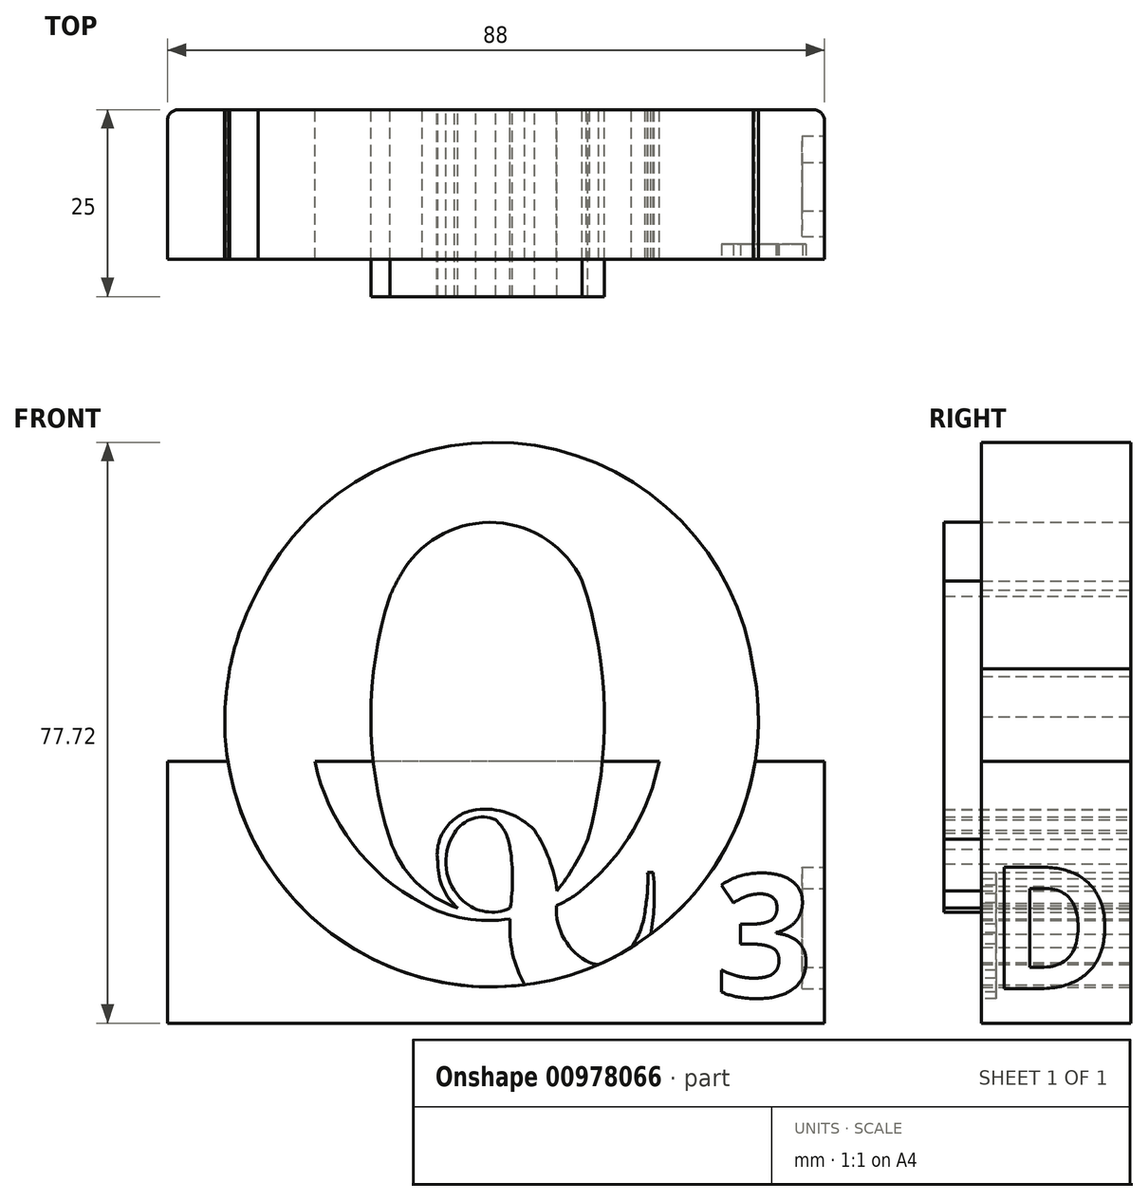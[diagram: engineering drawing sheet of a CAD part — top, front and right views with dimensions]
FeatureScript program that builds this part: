
annotation { "Feature Type Name" : "Feature", "Feature Type Description" : "" }
export const myFeature = defineFeature(function(context is Context, id is Id, definition is map)
    precondition{}
    {
        {
            var Q0;
            Q0=qCreatedBy(makeId("Front.planeOp"),FACE);
            var sketch = newSketch(context, id + "F0", { "sketchPlane" : qUnion([Q0])});
            skPoint(sketch, "E0.first.point", {"position": v(-8.97, 42.4) * mm});
            skPoint(sketch, "E0.second.point", {"position": v(4.84, -31.38) * mm});
            skPoint(sketch, "E0.third.point", {"position": v(40.23, 13.72) * mm});
            skArc(sketch, "E1", {"start": v(0, 43.7) * mm, "mid": v(-36.34, 3.66) * mm, "end": v(4.84, -31.38) * mm});
            skArc(sketch, "E2", {"start": v(20.57, -24) * mm, "mid": v(33.91, 17.02) * mm, "end": v(0, 43.7) * mm});
            skArc(sketch, "E3", {"start": v(-12, 29.47) * mm, "mid": v(-24.84, 4.65) * mm, "end": v(-9.87, -18.96) * mm});
            skArc(sketch, "E4", {"start": v(12.09, 28.05) * mm, "mid": v(0.27, 32.56) * mm, "end": v(-12, 29.47) * mm});
            skArc(sketch, "E5", {"start": v(12.09, -16.68) * mm, "mid": v(22.4, 5.68) * mm, "end": v(12.09, 28.05) * mm});
            skArc(sketch, "E6", {"start": v(8.11, -19.25) * mm, "mid": v(10.22, -18.15) * mm, "end": v(12.09, -16.68) * mm});
            skArc(sketch, "E7", {"start": v(-9.87, -18.96) * mm, "mid": v(-4.16, -21) * mm, "end": v(1.9, -21.05) * mm});
            skArc(sketch, "E8", {"start": v(1.9, -21.05) * mm, "mid": v(2.44, -26.48) * mm, "end": v(4.84, -31.38) * mm});
            skArc(sketch, "E9", {"start": v(8.11, -19.25) * mm, "mid": v(9.16, -23.77) * mm, "end": v(12.57, -26.92) * mm});
            skArc(sketch, "E10", {"start": v(12.57, -26.92) * mm, "mid": v(15.38, -27) * mm, "end": v(17.7, -25.42) * mm});
            skArc(sketch, "E11", {"start": v(17.7, -25.42) * mm, "mid": v(19.27, -22.75) * mm, "end": v(19.99, -19.74) * mm});
            skArc(sketch, "E12", {"start": v(19.99, -19.74) * mm, "mid": v(20.3, -17.3) * mm, "end": v(20.33, -14.85) * mm});
            skLineSegment(sketch, "E13", {"start": v(20.33, -14.85) * mm, "end": v(21.05, -14.85) * mm});
            skArc(sketch, "E14", {"start": v(20.57, -24) * mm, "mid": v(21.16, -19.45) * mm, "end": v(21.05, -14.85) * mm});
            skArc(sketch, "E15", {"start": v(11.56, 24.17) * mm, "mid": v(0.05, 31.98) * mm, "end": v(-12.33, 25.65) * mm});
            skArc(sketch, "E16", {"start": v(-12.33, 25.65) * mm, "mid": v(-13.33, 23.93) * mm, "end": v(-14.2, 22.14) * mm});
            skArc(sketch, "E17", {"start": v(12.27, -10.4) * mm, "mid": v(14.51, 6.94) * mm, "end": v(11.56, 24.17) * mm});
            skArc(sketch, "E18", {"start": v(8.2, -17.28) * mm, "mid": v(10.48, -13.99) * mm, "end": v(12.27, -10.4) * mm});
            skArc(sketch, "E19", {"start": v(-14.2, 22.14) * mm, "mid": v(-16.74, 5.87) * mm, "end": v(-14.2, -10.4) * mm});
            skArc(sketch, "E20", {"start": v(-14.2, -10.4) * mm, "mid": v(-10.74, -16.1) * mm, "end": v(-5.08, -19.62) * mm});
            skArc(sketch, "E21.trimOffspring", {"start": v(21.12, -15.68) * mm, "mid": v(21.07, -15.26) * mm, "end": v(21.03, -14.85) * mm});
            skArc(sketch, "E22", {"start": v(-7.75, -13.7) * mm, "mid": v(-7.09, -16.96) * mm, "end": v(-5.08, -19.62) * mm});
            skArc(sketch, "E23", {"start": v(-2.67, -6.43) * mm, "mid": v(-6.77, -8.98) * mm, "end": v(-7.75, -13.7) * mm});
            skArc(sketch, "E24", {"start": v(5.17, -9.2) * mm, "mid": v(1.57, -6.89) * mm, "end": v(-2.67, -6.43) * mm});
            skArc(sketch, "E25", {"start": v(8.2, -17.28) * mm, "mid": v(7.13, -13.07) * mm, "end": v(5.17, -9.2) * mm});
            skArc(sketch, "E26", {"start": v(1.9, -19.62) * mm, "mid": v(2.22, -15.67) * mm, "end": v(1.9, -11.72) * mm});
            skArc(sketch, "E27", {"start": v(1.9, -11.72) * mm, "mid": v(1.3, -9.59) * mm, "end": v(0, -7.8) * mm});
            skArc(sketch, "E28", {"start": v(0, -7.8) * mm, "mid": v(-3.12, -7.64) * mm, "end": v(-5.56, -9.59) * mm});
            skPoint(sketch, "E28.endSnap0", {"position": v(1.3, -9.59) * mm});
            skArc(sketch, "E29", {"start": v(-5.56, -9.59) * mm, "mid": v(-6.65, -14.33) * mm, "end": v(-4.4, -18.65) * mm});
            skArc(sketch, "E30", {"start": v(-4.4, -18.65) * mm, "mid": v(-1.39, -20.08) * mm, "end": v(1.9, -19.62) * mm});
            skSolve(sketch);
        }
        {
            var Q0;
            Q0=qSketchRegion(id+"F0",true);
            extrude(context, id + "F1", {"entities" : qUnion([Q0]), "depth" : 25 * mm, "offsetDistance" : 25 * mm});
        }
        {
            var Q0;
            Q0=makeQuery(id+"F1.opExtrude","CAP_FACE",FACE,{"disambiguationData":[OSD([sQuery(id+"F0.wireOp",EDGE,"E1"),sQuery(id+"F0.wireOp",EDGE,"E2"),sQuery(id+"F0.wireOp",EDGE,"E3"),sQuery(id+"F0.wireOp",EDGE,"E4"),sQuery(id+"F0.wireOp",EDGE,"E5"),sQuery(id+"F0.wireOp",EDGE,"E6"),sQuery(id+"F0.wireOp",EDGE,"E7"),sQuery(id+"F0.wireOp",EDGE,"E8"),sQuery(id+"F0.wireOp",EDGE,"E9"),sQuery(id+"F0.wireOp",EDGE,"E10"),sQuery(id+"F0.wireOp",EDGE,"E11"),sQuery(id+"F0.wireOp",EDGE,"E12"),sQuery(id+"F0.wireOp",EDGE,"E13"),sQuery(id+"F0.wireOp",EDGE,"E14"),sQuery(id+"F0.wireOp",EDGE,"E21.trimOffspring")])],"isStart":true});
            var sketch = newSketch(context, id + "F2", { "sketchPlane" : qUnion([Q0])});
            skArc(sketch, "E31", {"start": v(0, 43.7) * mm, "mid": v(-35.47, 8.29) * mm, "end": v(-4.84, -31.38) * mm});
            skArc(sketch, "E32", {"start": v(-4.84, -31.38) * mm, "mid": v(36.41, 3.65) * mm, "end": v(0, 43.7) * mm});
            skSolve(sketch);
        }
        {
            var Q0;
            Q0=qCreatedBy(makeId("Top.planeOp"),FACE);
            var sketch = newSketch(context, id + "F3", { "sketchPlane" : qUnion([Q0])});
            skLineSegment(sketch, "E33.bottom", {"start": v(42.5, 0) * mm, "end": v(-42.5, 0) * mm});
            skLineSegment(sketch, "E33.top", {"start": v(44, -20) * mm, "end": v(-44, -20) * mm});
            skLineSegment(sketch, "E33.left", {"start": v(44, -1.5) * mm, "end": v(44, -20) * mm});
            skLineSegment(sketch, "E33.right", {"start": v(-44, -1.5) * mm, "end": v(-44, -20) * mm});
            skPoint(sketch, "E33.middle", {"position": v(0, 0) * mm});
            skPoint(sketch, "E34.visualSharp", {"position": v(-44, 0) * mm});
            skArc(sketch, "E34.filletArc", {"start": v(-42.5, 0) * mm, "mid": v(-43.56, -0.44) * mm, "end": v(-44, -1.5) * mm});
            skPoint(sketch, "E35.visualSharp", {"position": v(44, 0) * mm});
            skArc(sketch, "E35.filletArc", {"start": v(44, -1.5) * mm, "mid": v(43.56, -0.44) * mm, "end": v(42.5, 0) * mm});
            skPoint(sketch, "E36.visualSharp", {"position": v(-44, -20) * mm});
            skPoint(sketch, "E37.visualSharp", {"position": v(44, -20) * mm});
            skSolve(sketch);
        }
        {
            var Q0;
            {var subQ2=makeQuery(id+"F1.opExtrude","CAP_EDGE",EDGE,{"disambiguationData":[OSD([sQuery(id+"F0.wireOp",EDGE,"E1")])],"isStart":true});Q0=makeQuery(id+"F2.imprint","IMPRINT",FACE,{"disambiguationData":[TD([[makeQuery(id+"F2.imprint","IMPRINT",EDGE,{"derivedFrom":subQ2}),-1.0]])]});}
            var sketch = newSketch(context, id + "F4", { "sketchPlane" : qUnion([Q0])});
            skArc(sketch, "E38", {"start": v(-34.36, 14.08) * mm, "mid": v(-0.95, -30.7) * mm, "end": v(35.78, 11.4) * mm});
            skPoint(sketch, "E38.first.point", {"position": v(-35.42, 7.34) * mm});
            skPoint(sketch, "E38.second.point", {"position": v(36.29, 6.8) * mm});
            skPoint(sketch, "E38.third.point", {"position": v(13.08, -28.42) * mm});
            skArc(sketch, "E39", {"start": v(35.78, 11.4) * mm, "mid": v(1.86, 42.8) * mm, "end": v(-34.36, 14.08) * mm});
            skSolve(sketch);
        }
        {
            var Q0;
            Q0 = qSketchRegion(id + "F4", true);
            extrude(context, id + "F5", {"entities" : qUnion([Q0]), "oppositeDirection" : true, "depth" : 20 * mm, "offsetDistance" : 25 * mm});
        }
        {
            var Q0;
            Q0=makeQuery(id+"F2.imprint","IMPRINT",FACE,{"disambiguationData":[TD([[makeQuery(id+"F2.imprint","IMPRINT",EDGE,{"derivedFrom":makeQuery(id+"F1.opExtrude","CAP_EDGE",EDGE,{"disambiguationData":[OSD([sQuery(id+"F0.wireOp",EDGE,"E3")])],"isStart":true})}),-1.0]])]});
            var sketch = newSketch(context, id + "F6", { "sketchPlane" : qUnion([Q0])});
            skArc(sketch, "E40", {"start": v(-34.48, 12.42) * mm, "mid": v(6.18, -29.73) * mm, "end": v(31.8, 22.93) * mm});
            skPoint(sketch, "E40.first.point", {"position": v(-31.53, 21.22) * mm});
            skPoint(sketch, "E40.second.point", {"position": v(36.14, 2.02) * mm});
            skPoint(sketch, "E40.third.point", {"position": v(0, -30.16) * mm});
            skArc(sketch, "E41", {"start": v(31.8, 22.93) * mm, "mid": v(-5.24, 42.3) * mm, "end": v(-34.48, 12.42) * mm});
            skCircle(sketch, "E42", {"center": v(0.59, 5.56) * mm, "radius": 47.39 * mm});
            skSolve(sketch);
        }
        {
            var Q0;
            Q0 = qSketchRegion(id + "F6", true);
            extrude(context, id + "F7", {"entities" : qUnion([Q0]), "operationType" : NewBodyOperationType.REMOVE, "oppositeDirection" : true, "depth" : 35 * mm, "offsetDistance" : 25 * mm});
        }
        {
            var Q0;
            Q0=qSketchRegion(id+"F3",true);
            extrude(context, id + "F8", {"entities" : qUnion([Q0]), "oppositeDirection" : true, "depth" : 35 * mm, "offsetDistance" : 25 * mm});
        }
        {
            var Q0;
            Q0=makeQuery(id+"F8.opExtrude","SWEPT_FACE",FACE,{"disambiguationData":[OSD([sQuery(id+"F3.wireOp",EDGE,"E33.left")])]});
            var sketch = newSketch(context, id + "F9", { "sketchPlane" : qUnion([Q0])});
            skText(sketch, "E43", { "text": "D", "fontName": "OpenSans-Bold.ttf"});
            const initialGuessF9  = {"E43": [-0.019, -0.03038, 1, 0, 0.01638]};
            skSetInitialGuess(sketch, initialGuessF9);
            skSolve(sketch);
        }
        {
            var Q0;
            Q0=qSketchRegion(id+"F9",true);
            extrude(context, id + "F10", {"entities" : qUnion([Q0]), "operationType" : NewBodyOperationType.REMOVE, "oppositeDirection" : true, "depth" : 3 * mm, "offsetDistance" : 25 * mm});
        }
        {
            var Q0;
            Q0=makeQuery(id+"F8.opExtrude","SWEPT_FACE",FACE,{"disambiguationData":[OSD([sQuery(id+"F3.wireOp",EDGE,"E33.top")])]});
            var sketch = newSketch(context, id + "F11", { "sketchPlane" : qUnion([Q0])});
            skText(sketch, "E44", { "text": "3", "fontName": "OpenSans-Bold.ttf"});
            const initialGuessF11  = {"E44": [0.02932, -0.0315, 1, 0, 0.0165]};
            skSetInitialGuess(sketch, initialGuessF11);
            skSolve(sketch);
        }
        {
            var Q0;
            Q0 = qSketchRegion(id + "F11", true);
            extrude(context, id + "F12", {"entities" : qUnion([Q0]), "operationType" : NewBodyOperationType.REMOVE, "oppositeDirection" : true, "depth" : 2 * mm, "offsetDistance" : 25 * mm});
        }
        {
            var Q0;
            Q0=makeQuery(id+"F1.opExtrude","SWEPT_BODY",BODY,{"disambiguationData":[OSD([sQuery(id+"F0.wireOp",EDGE,"E1"),sQuery(id+"F0.wireOp",EDGE,"E2"),sQuery(id+"F0.wireOp",EDGE,"E3"),sQuery(id+"F0.wireOp",EDGE,"E4"),sQuery(id+"F0.wireOp",EDGE,"E5"),sQuery(id+"F0.wireOp",EDGE,"E6"),sQuery(id+"F0.wireOp",EDGE,"E7"),sQuery(id+"F0.wireOp",EDGE,"E8"),sQuery(id+"F0.wireOp",EDGE,"E9"),sQuery(id+"F0.wireOp",EDGE,"E10"),sQuery(id+"F0.wireOp",EDGE,"E11"),sQuery(id+"F0.wireOp",EDGE,"E12"),sQuery(id+"F0.wireOp",EDGE,"E13"),sQuery(id+"F0.wireOp",EDGE,"E14"),sQuery(id+"F0.wireOp",EDGE,"E21.trimOffspring")])]});
            var Q1;
            Q1=makeQuery(id+"F8.opExtrude","SWEPT_BODY",BODY,{"disambiguationData":[OSD([sQuery(id+"F3.wireOp",EDGE,"E33.bottom"),sQuery(id+"F3.wireOp",EDGE,"E33.top"),sQuery(id+"F3.wireOp",EDGE,"E33.left"),sQuery(id+"F3.wireOp",EDGE,"E33.right"),sQuery(id+"F3.wireOp",EDGE,"E34.filletArc"),sQuery(id+"F3.wireOp",EDGE,"E35.filletArc")])]});
            booleanBodies(context, id + "F13", {"operationType" : BooleanOperationType.SUBTRACTION, "tools" : qUnion([Q0]), "targets" : qUnion([Q1])});
        }
    });
